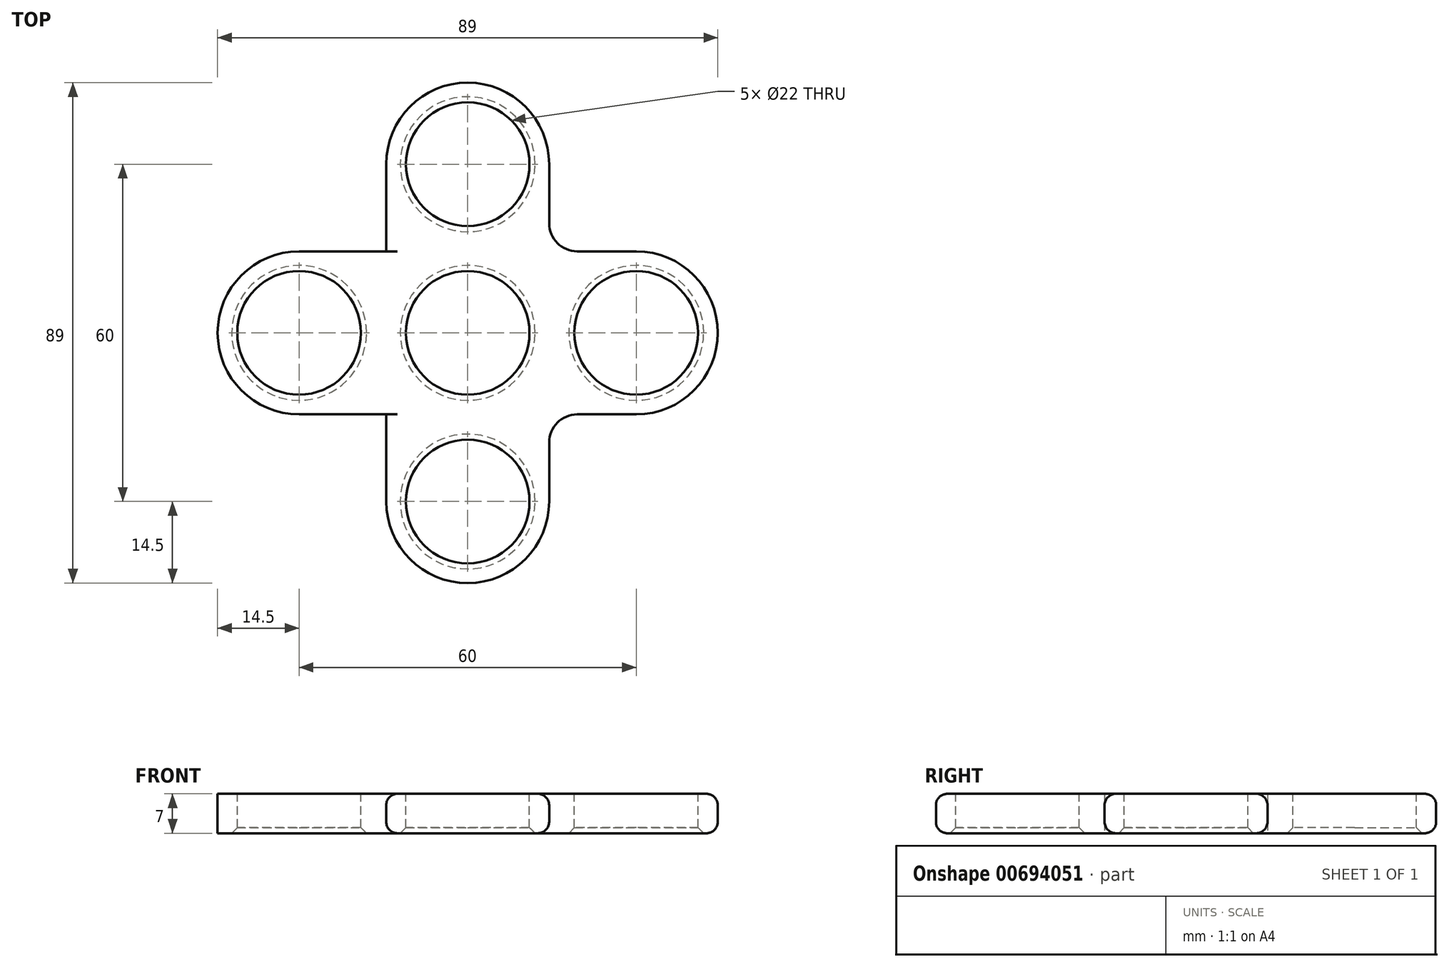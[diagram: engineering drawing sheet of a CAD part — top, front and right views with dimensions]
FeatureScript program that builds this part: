
annotation { "Feature Type Name" : "Feature", "Feature Type Description" : "" }
export const myFeature = defineFeature(function(context is Context, id is Id, definition is map)
    precondition{}
    {
        {
            var Q0;
            Q0=qCreatedBy(makeId("Top.planeOp"),FACE);
            var sketch = newSketch(context, id + "F0", { "sketchPlane" : qUnion([Q0])});
            skCircle(sketch, "E0", {"center": v(0, 0) * mm, "radius": 14.5 * mm});
            skCircle(sketch, "E1", {"center": v(0, -30) * mm, "radius": 14.5 * mm});
            skLineSegment(sketch, "E2", {"start": v(14.5, 0) * mm, "end": v(14.5, -30) * mm});
            skLineSegment(sketch, "E3", {"start": v(-14.5, 0) * mm, "end": v(-14.5, -30) * mm});
            skSolve(sketch);
        }
        {
            var Q0;
            Q0=qSketchRegion(id+"F0",true);
            var Q1;
            {var subQ0=sQuery(id+"F0.wireOp",EDGE,"E1");var subQ1=sQuery(id+"F0.wireOp",EDGE,"E0");var subQ2=makeQuery(id+"F0.imprint","INTERSECT",VERTEX,{"disambiguationData":[OD(0.0)],"derivedFrom":[subQ1,subQ0]});Q1=makeQuery(id+"F0.imprint","IMPRINT",FACE,{"disambiguationData":[TD([[makeQuery(id+"F0.imprint","IMPRINT",EDGE,{"disambiguationData":[TD([[subQ2,-1.0]])],"derivedFrom":subQ1}),1.0]])]});}
            extrude(context, id + "F1", {"entities" : qUnion([Q0, Q1]), "depth" : 7 * mm, "offsetDistance" : 25 * mm});
        }
        {
            var Q0;
            Q0=makeQuery(id+"F1.opExtrude","CAP_FACE",FACE,{"disambiguationData":[OSD([sQuery(id+"F0.wireOp",EDGE,"E0"),sQuery(id+"F0.wireOp",EDGE,"E1"),sQuery(id+"F0.wireOp",EDGE,"E2"),sQuery(id+"F0.wireOp",EDGE,"E3")])],"isStart":false});
            var sketch = newSketch(context, id + "F2", { "sketchPlane" : qUnion([Q0])});
            skCircle(sketch, "E4", {"center": v(0, 0) * mm, "radius": 11 * mm});
            skCircle(sketch, "E5", {"center": v(0, -30) * mm, "radius": 11 * mm});
            skLineSegment(sketch, "E6", {"start": v(0, 0) * mm, "end": v(0, -30) * mm});
            skSolve(sketch);
        }
        {
            var Q0;
            Q0=qSketchRegion(id+"F2",true);
            extrude(context, id + "F3", {"entities" : qUnion([Q0]), "operationType" : NewBodyOperationType.REMOVE, "endBound" : BoundingType.THROUGH_ALL, "oppositeDirection" : true, "depth" : 25 * mm, "offsetDistance" : 25 * mm});
        }
        {
            var Q0;
            Q0=qCreatedBy(makeId("Front.planeOp"),FACE);
            var sketch = newSketch(context, id + "F4", { "sketchPlane" : qUnion([Q0])});
            skLineSegment(sketch, "E7", {"start": v(0, 0) * mm, "end": v(0, 26.48) * mm});
            skSolve(sketch);
        }
        {
            var Q0;
            Q0=makeQuery(id+"F1.opExtrude","SWEPT_BODY",BODY,{"disambiguationData":[OSD([sQuery(id+"F0.wireOp",EDGE,"E0"),sQuery(id+"F0.wireOp",EDGE,"E1"),sQuery(id+"F0.wireOp",EDGE,"E2"),sQuery(id+"F0.wireOp",EDGE,"E3")])]});
            var Q1;
            Q1=sQuery(id+"F4.wireOp",EDGE,"E7");
            circularPattern(context, id + "F5", {"entities" : qUnion([Q0]), "axis" : qUnion([Q1]), "angle" : 360 * degree, "instanceCount" : 4, "equalSpace" : true});
        }
        {
            var Q0;
            Q0=makeQuery(id+"F5.opPattern","COPY",BODY,{"derivedFrom":makeQuery(id+"F1.opExtrude","SWEPT_BODY",BODY,{"disambiguationData":[OSD([sQuery(id+"F0.wireOp",EDGE,"E0"),sQuery(id+"F0.wireOp",EDGE,"E1"),sQuery(id+"F0.wireOp",EDGE,"E2"),sQuery(id+"F0.wireOp",EDGE,"E3")])]}),"instanceName":"4"});
            var Q1;
            Q1=makeQuery(id+"F5.opPattern","COPY",BODY,{"derivedFrom":makeQuery(id+"F1.opExtrude","SWEPT_BODY",BODY,{"disambiguationData":[OSD([sQuery(id+"F0.wireOp",EDGE,"E0"),sQuery(id+"F0.wireOp",EDGE,"E1"),sQuery(id+"F0.wireOp",EDGE,"E2"),sQuery(id+"F0.wireOp",EDGE,"E3")])]}),"instanceName":"3"});
            var Q2;
            Q2=makeQuery(id+"F5.opPattern","COPY",BODY,{"derivedFrom":makeQuery(id+"F1.opExtrude","SWEPT_BODY",BODY,{"disambiguationData":[OSD([sQuery(id+"F0.wireOp",EDGE,"E0"),sQuery(id+"F0.wireOp",EDGE,"E1"),sQuery(id+"F0.wireOp",EDGE,"E2"),sQuery(id+"F0.wireOp",EDGE,"E3")])]}),"instanceName":"2"});
            var Q3;
            Q3=makeQuery(id+"F5.opPattern","COPY",BODY,{"derivedFrom":makeQuery(id+"F1.opExtrude","SWEPT_BODY",BODY,{"disambiguationData":[OSD([sQuery(id+"F0.wireOp",EDGE,"E0"),sQuery(id+"F0.wireOp",EDGE,"E1"),sQuery(id+"F0.wireOp",EDGE,"E2"),sQuery(id+"F0.wireOp",EDGE,"E3")])]}),"instanceName":"1"});
            var Q4;
            Q4=makeQuery(id+"F1.opExtrude","SWEPT_BODY",BODY,{"disambiguationData":[OSD([sQuery(id+"F0.wireOp",EDGE,"E0"),sQuery(id+"F0.wireOp",EDGE,"E1"),sQuery(id+"F0.wireOp",EDGE,"E2"),sQuery(id+"F0.wireOp",EDGE,"E3")])]});
            var Q5;
            Q5=makeQuery(id+"F5.opPattern","COPY",BODY,{"derivedFrom":makeQuery(id+"F1.opExtrude","SWEPT_BODY",BODY,{"disambiguationData":[OSD([sQuery(id+"F0.wireOp",EDGE,"E0"),sQuery(id+"F0.wireOp",EDGE,"E1"),sQuery(id+"F0.wireOp",EDGE,"E2"),sQuery(id+"F0.wireOp",EDGE,"E3")])]}),"instanceName":"5"});
            booleanBodies(context, id + "F6", {"operationType" : BooleanOperationType.UNION, "tools" : qUnion([Q0, Q1, Q2, Q3, Q4, Q5])});
        }
        {
            var Q0;
            Q0=makeQuery(id+"F6.opBoolean","INTERSECT",EDGE,{"derivedFrom":[makeQuery(id+"F5.opPattern","COPY",FACE,{"derivedFrom":makeQuery(id+"F1.opExtrude","SWEPT_FACE",FACE,{"disambiguationData":[OSD([sQuery(id+"F0.wireOp",EDGE,"E2")])]}),"instanceName":"4"}),makeQuery(id+"F5.opPattern","COPY",FACE,{"derivedFrom":makeQuery(id+"F1.opExtrude","SWEPT_FACE",FACE,{"disambiguationData":[OSD([sQuery(id+"F0.wireOp",EDGE,"E3")])]}),"instanceName":"5"})]});
            var Q1;
            Q1=makeQuery(id+"F6.opBoolean","INTERSECT",EDGE,{"derivedFrom":[makeQuery(id+"F1.opExtrude","SWEPT_FACE",FACE,{"disambiguationData":[OSD([sQuery(id+"F0.wireOp",EDGE,"E3")])]}),makeQuery(id+"F5.opPattern","COPY",FACE,{"derivedFrom":makeQuery(id+"F1.opExtrude","SWEPT_FACE",FACE,{"disambiguationData":[OSD([sQuery(id+"F0.wireOp",EDGE,"E2")])]}),"instanceName":"5"})]});
            var Q2;
            Q2=makeQuery(id+"F6.opBoolean","INTERSECT",EDGE,{"derivedFrom":[makeQuery(id+"F1.opExtrude","SWEPT_FACE",FACE,{"disambiguationData":[OSD([sQuery(id+"F0.wireOp",EDGE,"E2")])]}),makeQuery(id+"F5.opPattern","COPY",FACE,{"derivedFrom":makeQuery(id+"F1.opExtrude","SWEPT_FACE",FACE,{"disambiguationData":[OSD([sQuery(id+"F0.wireOp",EDGE,"E3")])]}),"instanceName":"1"})]});
            var Q3;
            Q3=makeQuery(id+"F6.opBoolean","INTERSECT",EDGE,{"derivedFrom":[makeQuery(id+"F5.opPattern","COPY",FACE,{"derivedFrom":makeQuery(id+"F1.opExtrude","SWEPT_FACE",FACE,{"disambiguationData":[OSD([sQuery(id+"F0.wireOp",EDGE,"E2")])]}),"instanceName":"1"}),makeQuery(id+"F5.opPattern","COPY",FACE,{"derivedFrom":makeQuery(id+"F1.opExtrude","SWEPT_FACE",FACE,{"disambiguationData":[OSD([sQuery(id+"F0.wireOp",EDGE,"E3")])]}),"instanceName":"2"})]});
            var Q4;
            {var subQ0=makeQuery(id+"F1.opExtrude","SWEPT_FACE",FACE,{"disambiguationData":[OSD([sQuery(id+"F0.wireOp",EDGE,"E3")])]});Q4=makeQuery(id+"F6.opBoolean","INTERSECT",EDGE,{"derivedFrom":[makeQuery(id+"F5.opPattern","COPY",FACE,{"derivedFrom":subQ0,"instanceName":"3"}),makeQuery(id+"F5.opPattern","COPY",FACE,{"derivedFrom":subQ0,"instanceName":"5"})]});}
            var Q5;
            Q5=makeQuery(id+"F6.opBoolean","INTERSECT",EDGE,{"derivedFrom":[makeQuery(id+"F5.opPattern","COPY",FACE,{"derivedFrom":makeQuery(id+"F1.opExtrude","SWEPT_FACE",FACE,{"disambiguationData":[OSD([sQuery(id+"F0.wireOp",EDGE,"E2")])]}),"instanceName":"3"}),makeQuery(id+"F5.opPattern","COPY",FACE,{"derivedFrom":makeQuery(id+"F1.opExtrude","SWEPT_FACE",FACE,{"disambiguationData":[OSD([sQuery(id+"F0.wireOp",EDGE,"E3")])]}),"instanceName":"4"})]});
            fillet(context, id + "F7", {"entities" : qUnion([Q0, Q1, Q2, Q3, Q4, Q5]), "radius" : 5 * mm, "tangentPropagation" : true, "allowEdgeOverflow" : false});
        }
        {
            var Q0;
            Q0=makeQuery(id+"F5.opPattern","COPY",EDGE,{"derivedFrom":makeQuery(id+"F1.opExtrude","CAP_EDGE",EDGE,{"disambiguationData":[OSD([sQuery(id+"F0.wireOp",EDGE,"E1")])],"isStart":false}),"instanceName":"1"});
            var Q1;
            Q1=makeQuery(id+"F1.opExtrude","CAP_EDGE",EDGE,{"disambiguationData":[OSD([sQuery(id+"F0.wireOp",EDGE,"E1")])],"isStart":true});
            fillet(context, id + "F8", {"entities" : qUnion([Q0, Q1]), "radius" : 2 * mm, "tangentPropagation" : true, "allowEdgeOverflow" : false});
        }
        {
            var Q0;
            Q0=makeQuery(id+"F5.opPattern","COPY",EDGE,{"derivedFrom":makeQuery(id+"F3.boolean.opBoolean","COPY",EDGE,{"derivedFrom":makeQuery(id+"F3.opExtrude","CAP_EDGE",EDGE,{"disambiguationData":[OSD([sQuery(id+"F2.wireOp",EDGE,"E4")])],"isStart":true})}),"instanceName":"4"});
            var Q1;
            Q1=makeQuery(id+"F5.opPattern","COPY",EDGE,{"derivedFrom":makeQuery(id+"F3.boolean.opBoolean","COPY",EDGE,{"derivedFrom":makeQuery(id+"F3.opExtrude","CAP_EDGE",EDGE,{"disambiguationData":[OSD([sQuery(id+"F2.wireOp",EDGE,"E5")])],"isStart":true})}),"instanceName":"2"});
            var Q2;
            Q2=makeQuery(id+"F5.opPattern","COPY",EDGE,{"derivedFrom":makeQuery(id+"F3.boolean.opBoolean","COPY",EDGE,{"derivedFrom":makeQuery(id+"F3.opExtrude","CAP_EDGE",EDGE,{"disambiguationData":[OSD([sQuery(id+"F2.wireOp",EDGE,"E5")])],"isStart":true})}),"instanceName":"3"});
            var Q3;
            Q3=makeQuery(id+"F5.opPattern","COPY",EDGE,{"derivedFrom":makeQuery(id+"F3.boolean.opBoolean","COPY",EDGE,{"derivedFrom":makeQuery(id+"F3.opExtrude","CAP_EDGE",EDGE,{"disambiguationData":[OSD([sQuery(id+"F2.wireOp",EDGE,"E5")])],"isStart":true})}),"instanceName":"4"});
            var Q4;
            Q4=makeQuery(id+"F5.opPattern","COPY",EDGE,{"derivedFrom":makeQuery(id+"F3.boolean.opBoolean","COPY",EDGE,{"derivedFrom":makeQuery(id+"F3.opExtrude","CAP_EDGE",EDGE,{"disambiguationData":[OSD([sQuery(id+"F2.wireOp",EDGE,"E5")])],"isStart":true})}),"instanceName":"5"});
            var Q5;
            Q5=makeQuery(id+"F3.boolean.opBoolean","COPY",EDGE,{"derivedFrom":makeQuery(id+"F3.opExtrude","CAP_EDGE",EDGE,{"disambiguationData":[OSD([sQuery(id+"F2.wireOp",EDGE,"E5")])],"isStart":true})});
            var Q6;
            Q6=makeQuery(id+"F5.opPattern","COPY",EDGE,{"derivedFrom":makeQuery(id+"F3.boolean.opBoolean","COPY",EDGE,{"derivedFrom":makeQuery(id+"F3.opExtrude","CAP_EDGE",EDGE,{"disambiguationData":[OSD([sQuery(id+"F2.wireOp",EDGE,"E5")])],"isStart":true})}),"instanceName":"1"});
            var Q7;
            Q7=makeQuery(id+"F5.opPattern","COPY",EDGE,{"derivedFrom":makeQuery(id+"F3.boolean.opBoolean","INTERSECT",EDGE,{"derivedFrom":[makeQuery(id+"F1.opExtrude","CAP_FACE",FACE,{"disambiguationData":[OSD([sQuery(id+"F0.wireOp",EDGE,"E0"),sQuery(id+"F0.wireOp",EDGE,"E1"),sQuery(id+"F0.wireOp",EDGE,"E2"),sQuery(id+"F0.wireOp",EDGE,"E3")])],"isStart":true}),makeQuery(id+"F3.opExtrude","SWEPT_FACE",FACE,{"disambiguationData":[OSD([sQuery(id+"F2.wireOp",EDGE,"E5")])]})]}),"instanceName":"5"});
            var Q8;
            Q8=makeQuery(id+"F3.boolean.opBoolean","INTERSECT",EDGE,{"derivedFrom":[makeQuery(id+"F1.opExtrude","CAP_FACE",FACE,{"disambiguationData":[OSD([sQuery(id+"F0.wireOp",EDGE,"E0"),sQuery(id+"F0.wireOp",EDGE,"E1"),sQuery(id+"F0.wireOp",EDGE,"E2"),sQuery(id+"F0.wireOp",EDGE,"E3")])],"isStart":true}),makeQuery(id+"F3.opExtrude","SWEPT_FACE",FACE,{"disambiguationData":[OSD([sQuery(id+"F2.wireOp",EDGE,"E5")])]})]});
            var Q9;
            Q9=makeQuery(id+"F5.opPattern","COPY",EDGE,{"derivedFrom":makeQuery(id+"F3.boolean.opBoolean","INTERSECT",EDGE,{"derivedFrom":[makeQuery(id+"F1.opExtrude","CAP_FACE",FACE,{"disambiguationData":[OSD([sQuery(id+"F0.wireOp",EDGE,"E0"),sQuery(id+"F0.wireOp",EDGE,"E1"),sQuery(id+"F0.wireOp",EDGE,"E2"),sQuery(id+"F0.wireOp",EDGE,"E3")])],"isStart":true}),makeQuery(id+"F3.opExtrude","SWEPT_FACE",FACE,{"disambiguationData":[OSD([sQuery(id+"F2.wireOp",EDGE,"E5")])]})]}),"instanceName":"1"});
            var Q10;
            Q10=makeQuery(id+"F5.opPattern","COPY",EDGE,{"derivedFrom":makeQuery(id+"F3.boolean.opBoolean","INTERSECT",EDGE,{"derivedFrom":[makeQuery(id+"F1.opExtrude","CAP_FACE",FACE,{"disambiguationData":[OSD([sQuery(id+"F0.wireOp",EDGE,"E0"),sQuery(id+"F0.wireOp",EDGE,"E1"),sQuery(id+"F0.wireOp",EDGE,"E2"),sQuery(id+"F0.wireOp",EDGE,"E3")])],"isStart":true}),makeQuery(id+"F3.opExtrude","SWEPT_FACE",FACE,{"disambiguationData":[OSD([sQuery(id+"F2.wireOp",EDGE,"E5")])]})]}),"instanceName":"2"});
            var Q11;
            Q11=makeQuery(id+"F5.opPattern","COPY",EDGE,{"derivedFrom":makeQuery(id+"F3.boolean.opBoolean","INTERSECT",EDGE,{"derivedFrom":[makeQuery(id+"F1.opExtrude","CAP_FACE",FACE,{"disambiguationData":[OSD([sQuery(id+"F0.wireOp",EDGE,"E0"),sQuery(id+"F0.wireOp",EDGE,"E1"),sQuery(id+"F0.wireOp",EDGE,"E2"),sQuery(id+"F0.wireOp",EDGE,"E3")])],"isStart":true}),makeQuery(id+"F3.opExtrude","SWEPT_FACE",FACE,{"disambiguationData":[OSD([sQuery(id+"F2.wireOp",EDGE,"E5")])]})]}),"instanceName":"3"});
            var Q12;
            Q12=makeQuery(id+"F5.opPattern","COPY",EDGE,{"derivedFrom":makeQuery(id+"F3.boolean.opBoolean","INTERSECT",EDGE,{"derivedFrom":[makeQuery(id+"F1.opExtrude","CAP_FACE",FACE,{"disambiguationData":[OSD([sQuery(id+"F0.wireOp",EDGE,"E0"),sQuery(id+"F0.wireOp",EDGE,"E1"),sQuery(id+"F0.wireOp",EDGE,"E2"),sQuery(id+"F0.wireOp",EDGE,"E3")])],"isStart":true}),makeQuery(id+"F3.opExtrude","SWEPT_FACE",FACE,{"disambiguationData":[OSD([sQuery(id+"F2.wireOp",EDGE,"E4")])]})]}),"instanceName":"4"});
            var Q13;
            Q13=makeQuery(id+"F5.opPattern","COPY",EDGE,{"derivedFrom":makeQuery(id+"F3.boolean.opBoolean","INTERSECT",EDGE,{"derivedFrom":[makeQuery(id+"F1.opExtrude","CAP_FACE",FACE,{"disambiguationData":[OSD([sQuery(id+"F0.wireOp",EDGE,"E0"),sQuery(id+"F0.wireOp",EDGE,"E1"),sQuery(id+"F0.wireOp",EDGE,"E2"),sQuery(id+"F0.wireOp",EDGE,"E3")])],"isStart":true}),makeQuery(id+"F3.opExtrude","SWEPT_FACE",FACE,{"disambiguationData":[OSD([sQuery(id+"F2.wireOp",EDGE,"E5")])]})]}),"instanceName":"4"});
            var Q14;
            Q14=makeQuery(id+"F5.opPattern","COPY",EDGE,{"derivedFrom":makeQuery(id+"F3.boolean.opBoolean","INTERSECT",EDGE,{"derivedFrom":[makeQuery(id+"F1.opExtrude","CAP_FACE",FACE,{"disambiguationData":[OSD([sQuery(id+"F0.wireOp",EDGE,"E0"),sQuery(id+"F0.wireOp",EDGE,"E1"),sQuery(id+"F0.wireOp",EDGE,"E2"),sQuery(id+"F0.wireOp",EDGE,"E3")])],"isStart":true}),makeQuery(id+"F3.opExtrude","SWEPT_FACE",FACE,{"disambiguationData":[OSD([sQuery(id+"F2.wireOp",EDGE,"E4")])]})]}),"instanceName":"3"});
            var Q15;
            Q15=makeQuery(id+"F5.opPattern","COPY",EDGE,{"derivedFrom":makeQuery(id+"F3.boolean.opBoolean","COPY",EDGE,{"derivedFrom":makeQuery(id+"F3.opExtrude","CAP_EDGE",EDGE,{"disambiguationData":[OSD([sQuery(id+"F2.wireOp",EDGE,"E4")])],"isStart":true})}),"instanceName":"3"});
            chamfer(context, id + "F9", {"entities" : qUnion([Q0, Q1, Q2, Q3, Q4, Q5, Q6, Q7, Q8, Q9, Q10, Q11, Q12, Q13, Q14, Q15]), "width" : 1 * mm, "tangentPropagation" : true});
        }
    });
